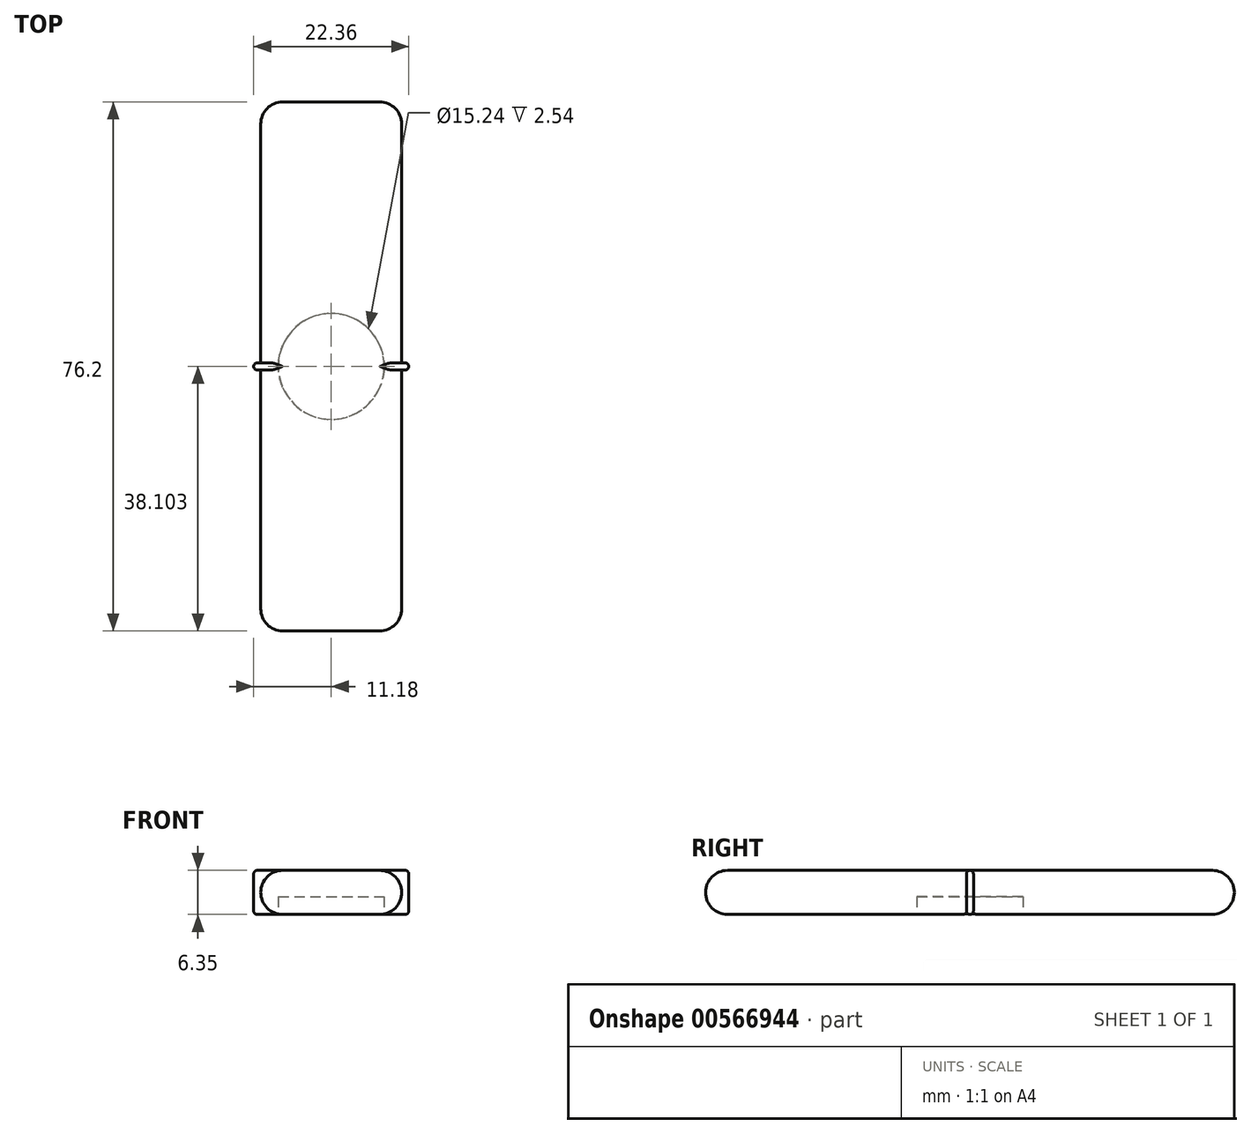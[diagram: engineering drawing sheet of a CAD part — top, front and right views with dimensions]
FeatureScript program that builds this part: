
annotation { "Feature Type Name" : "Feature", "Feature Type Description" : "" }
export const myFeature = defineFeature(function(context is Context, id is Id, definition is map)
    precondition{}
    {
        {
            var Q0;
            Q0=qCreatedBy(makeId("Top.planeOp"),FACE);
            var sketch = newSketch(context, id + "F0", { "sketchPlane" : qUnion([Q0])});
            skLineSegment(sketch, "E0.bottom", {"start": v(0, 45.34) * mm, "end": v(-20.32, 45.34) * mm});
            skLineSegment(sketch, "E0.top", {"start": v(0, -30.86) * mm, "end": v(-20.32, -30.86) * mm});
            skLineSegment(sketch, "E0.left", {"start": v(0, 45.34) * mm, "end": v(0, 7.75) * mm});
            skLineSegment(sketch, "E0.right", {"start": v(-20.32, 45.34) * mm, "end": v(-20.32, 7.75) * mm});
            skLineSegment(sketch, "E1", {"start": v(-20.32, 7.24) * mm, "end": v(-22.35, 7.24) * mm, "construction": true});
            skLineSegment(sketch, "E2", {"start": v(-20.32, 7.75) * mm, "end": v(-21.34, 7.75) * mm});
            skPoint(sketch, "E2.endSnap0", {"position": v(-21.34, 7.24) * mm});
            skLineSegment(sketch, "E3", {"start": v(-21.34, 7.75) * mm, "end": v(-21.34, 6.74) * mm});
            skLineSegment(sketch, "E4", {"start": v(-21.34, 6.74) * mm, "end": v(-20.32, 6.74) * mm});
            skLineSegment(sketch, "E5", {"start": v(-10.16, 45.34) * mm, "end": v(-10.16, -30.86) * mm, "construction": true});
            skLineSegment(sketch, "E6.MirrorCS", {"start": v(0, 7.75) * mm, "end": v(1.02, 7.75) * mm});
            skLineSegment(sketch, "E7.MirrorCS", {"start": v(1.02, 7.75) * mm, "end": v(1.02, 6.74) * mm});
            skLineSegment(sketch, "E8.MirrorCS", {"start": v(1.02, 6.74) * mm, "end": v(0, 6.74) * mm});
            skLineSegment(sketch, "E9.trimOffspring", {"start": v(-20.32, 6.74) * mm, "end": v(-20.32, -30.86) * mm});
            skLineSegment(sketch, "E10.trimOffspring", {"start": v(0, 6.74) * mm, "end": v(0, -30.86) * mm});
            skSolve(sketch);
        }
        {
            var Q0;
            Q0 = qSketchRegion(id + "F0", true);
            extrude(context, id + "F1", {"entities" : qUnion([Q0]), "depth" : 6.35 * mm, "offsetDistance" : 25.4 * mm});
        }
        {
            var Q0;
            Q0=makeQuery(id+"F1.opExtrude","SWEPT_FACE",FACE,{"disambiguationData":[OSD([sQuery(id+"F0.wireOp",EDGE,"E7.MirrorCS")])]});
            var Q1;
            Q1=makeQuery(id+"F1.opExtrude","CAP_EDGE",EDGE,{"disambiguationData":[OSD([sQuery(id+"F0.wireOp",EDGE,"E6.MirrorCS")])],"isStart":false});
            var Q2;
            Q2=makeQuery(id+"F1.opExtrude","CAP_EDGE",EDGE,{"disambiguationData":[OSD([sQuery(id+"F0.wireOp",EDGE,"E8.MirrorCS")])],"isStart":false});
            var Q3;
            Q3=makeQuery(id+"F1.opExtrude","CAP_EDGE",EDGE,{"disambiguationData":[OSD([sQuery(id+"F0.wireOp",EDGE,"E8.MirrorCS")])],"isStart":true});
            var Q4;
            Q4=makeQuery(id+"F1.opExtrude","CAP_EDGE",EDGE,{"disambiguationData":[OSD([sQuery(id+"F0.wireOp",EDGE,"E6.MirrorCS")])],"isStart":true});
            var Q5;
            Q5=makeQuery(id+"F1.opExtrude","SWEPT_FACE",FACE,{"disambiguationData":[OSD([sQuery(id+"F0.wireOp",EDGE,"E3")])]});
            var Q6;
            Q6=makeQuery(id+"F1.opExtrude","CAP_EDGE",EDGE,{"disambiguationData":[OSD([sQuery(id+"F0.wireOp",EDGE,"E3")])],"isStart":false});
            var Q7;
            Q7=makeQuery(id+"F1.opExtrude","CAP_EDGE",EDGE,{"disambiguationData":[OSD([sQuery(id+"F0.wireOp",EDGE,"E2")])],"isStart":false});
            var Q8;
            Q8=makeQuery(id+"F1.opExtrude","CAP_EDGE",EDGE,{"disambiguationData":[OSD([sQuery(id+"F0.wireOp",EDGE,"E4")])],"isStart":false});
            var Q9;
            Q9=makeQuery(id+"F1.opExtrude","CAP_EDGE",EDGE,{"disambiguationData":[OSD([sQuery(id+"F0.wireOp",EDGE,"E2")])],"isStart":true});
            var Q10;
            Q10=makeQuery(id+"F1.opExtrude","CAP_EDGE",EDGE,{"disambiguationData":[OSD([sQuery(id+"F0.wireOp",EDGE,"E4")])],"isStart":true});
            fillet(context, id + "F2", {"entities" : qUnion([Q0, Q1, Q2, Q3, Q4, Q5, Q6, Q7, Q8, Q9, Q10]), "radius" : 0.5 * mm, "tangentPropagation" : true, "allowEdgeOverflow" : false});
        }
        {
            var Q0;
            Q0=makeQuery(id+"F1.opExtrude","SWEPT_EDGE",EDGE,{"disambiguationData":[OSD([sQuery(id+"F0.wireOp",EDGE,"E0.top"),sQuery(id+"F0.wireOp",EDGE,"E10.trimOffspring")])]});
            var Q1;
            Q1=makeQuery(id+"F1.opExtrude","SWEPT_EDGE",EDGE,{"disambiguationData":[OSD([sQuery(id+"F0.wireOp",EDGE,"E0.top"),sQuery(id+"F0.wireOp",EDGE,"E9.trimOffspring")])]});
            var Q2;
            Q2=makeQuery(id+"F1.opExtrude","SWEPT_EDGE",EDGE,{"disambiguationData":[OSD([sQuery(id+"F0.wireOp",EDGE,"E0.bottom"),sQuery(id+"F0.wireOp",EDGE,"E0.right")])]});
            var Q3;
            Q3=makeQuery(id+"F1.opExtrude","SWEPT_EDGE",EDGE,{"disambiguationData":[OSD([sQuery(id+"F0.wireOp",EDGE,"E0.bottom"),sQuery(id+"F0.wireOp",EDGE,"E0.left")])]});
            var Q4;
            Q4=makeQuery(id+"F1.opExtrude","CAP_EDGE",EDGE,{"disambiguationData":[OSD([sQuery(id+"F0.wireOp",EDGE,"E0.bottom")])],"isStart":false});
            var Q5;
            Q5=makeQuery(id+"F1.opExtrude","CAP_EDGE",EDGE,{"disambiguationData":[OSD([sQuery(id+"F0.wireOp",EDGE,"E0.bottom")])],"isStart":true});
            var Q6;
            Q6=makeQuery(id+"F1.opExtrude","CAP_EDGE",EDGE,{"disambiguationData":[OSD([sQuery(id+"F0.wireOp",EDGE,"E0.top")])],"isStart":false});
            var Q7;
            Q7=makeQuery(id+"F1.opExtrude","CAP_EDGE",EDGE,{"disambiguationData":[OSD([sQuery(id+"F0.wireOp",EDGE,"E0.top")])],"isStart":true});
            var Q8;
            Q8=makeQuery(id+"F1.opExtrude","CAP_EDGE",EDGE,{"disambiguationData":[OSD([sQuery(id+"F0.wireOp",EDGE,"E9.trimOffspring")])],"isStart":false});
            var Q9;
            Q9=makeQuery(id+"F1.opExtrude","CAP_EDGE",EDGE,{"disambiguationData":[OSD([sQuery(id+"F0.wireOp",EDGE,"E9.trimOffspring")])],"isStart":true});
            var Q10;
            Q10=makeQuery(id+"F1.opExtrude","CAP_EDGE",EDGE,{"disambiguationData":[OSD([sQuery(id+"F0.wireOp",EDGE,"E0.left")])],"isStart":true});
            var Q11;
            Q11=makeQuery(id+"F1.opExtrude","CAP_EDGE",EDGE,{"disambiguationData":[OSD([sQuery(id+"F0.wireOp",EDGE,"E0.left")])],"isStart":false});
            var Q12;
            Q12=makeQuery(id+"F1.opExtrude","CAP_EDGE",EDGE,{"disambiguationData":[OSD([sQuery(id+"F0.wireOp",EDGE,"E10.trimOffspring")])],"isStart":true});
            var Q13;
            Q13=makeQuery(id+"F1.opExtrude","CAP_EDGE",EDGE,{"disambiguationData":[OSD([sQuery(id+"F0.wireOp",EDGE,"E10.trimOffspring")])],"isStart":false});
            fillet(context, id + "F3", {"entities" : qUnion([Q0, Q1, Q2, Q3, Q4, Q5, Q6, Q7, Q8, Q9, Q10, Q11, Q12, Q13]), "radius" : 3.17 * mm, "tangentPropagation" : true, "allowEdgeOverflow" : false});
        }
        {
            var Q0;
            Q0=makeQuery(id+"F1.opExtrude","CAP_FACE",FACE,{"disambiguationData":[OSD([sQuery(id+"F0.wireOp",EDGE,"E0.bottom"),sQuery(id+"F0.wireOp",EDGE,"E0.top"),sQuery(id+"F0.wireOp",EDGE,"E0.left"),sQuery(id+"F0.wireOp",EDGE,"E0.right"),sQuery(id+"F0.wireOp",EDGE,"E2"),sQuery(id+"F0.wireOp",EDGE,"E3"),sQuery(id+"F0.wireOp",EDGE,"E4"),sQuery(id+"F0.wireOp",EDGE,"E6.MirrorCS"),sQuery(id+"F0.wireOp",EDGE,"E7.MirrorCS"),sQuery(id+"F0.wireOp",EDGE,"E8.MirrorCS"),sQuery(id+"F0.wireOp",EDGE,"E9.trimOffspring"),sQuery(id+"F0.wireOp",EDGE,"E10.trimOffspring")])],"isStart":true});
            var sketch = newSketch(context, id + "F4", { "sketchPlane" : qUnion([Q0])});
            skCircle(sketch, "E11", {"center": v(-10.16, -7.24) * mm, "radius": 7.62 * mm});
            skLineSegment(sketch, "E12", {"start": v(-17.15, -7.24) * mm, "end": v(-3.18, -7.24) * mm, "construction": true});
            skSolve(sketch);
        }
        {
            var Q0;
            Q0 = qSketchRegion(id + "F4", true);
            extrude(context, id + "F5", {"entities" : qUnion([Q0]), "operationType" : NewBodyOperationType.REMOVE, "oppositeDirection" : true, "depth" : 2.54 * mm, "offsetDistance" : 25.4 * mm});
        }
    });
